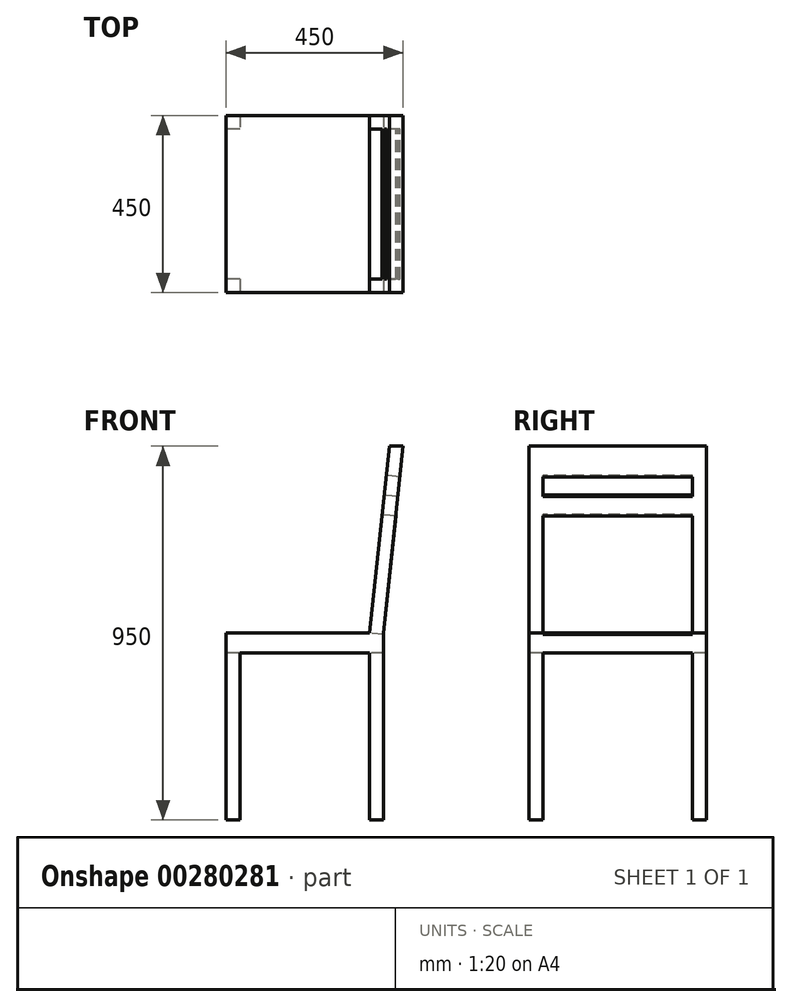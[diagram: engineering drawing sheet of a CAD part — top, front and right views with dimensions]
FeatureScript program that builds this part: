
annotation { "Feature Type Name" : "Feature", "Feature Type Description" : "" }
export const myFeature = defineFeature(function(context is Context, id is Id, definition is map)
    precondition{}
    {
        {
            var Q0;
            Q0=qCreatedBy(makeId("Top.planeOp"),FACE);
            var sketch = newSketch(context, id + "F0", { "sketchPlane" : qUnion([Q0])});
            skLineSegment(sketch, "E0.bottom", {"start": v(225, 225) * mm, "end": v(-225, 225) * mm});
            skLineSegment(sketch, "E0.top", {"start": v(225, -225) * mm, "end": v(-225, -225) * mm});
            skLineSegment(sketch, "E0.left", {"start": v(225, 225) * mm, "end": v(225, -225) * mm});
            skLineSegment(sketch, "E0.right", {"start": v(-225, 225) * mm, "end": v(-225, -225) * mm});
            skPoint(sketch, "E0.middle", {"position": v(0, 0) * mm});
            skSolve(sketch);
        }
        {
            var Q0;
            Q0=qSketchRegion(id+"F0",true);
            extrude(context, id + "F1", {"entities" : qUnion([Q0]), "depth" : 950 * mm});
        }
        {
            var Q0;
            Q0=makeQuery(id+"F1.opExtrude","SWEPT_FACE",FACE,{"disambiguationData":[OSD([sQuery(id+"F0.wireOp",EDGE,"E0.top")])]});
            var sketch = newSketch(context, id + "F2", { "sketchPlane" : qUnion([Q0])});
            skLineSegment(sketch, "E1.bottom", {"start": v(-225, 475) * mm, "end": v(225, 475) * mm});
            skLineSegment(sketch, "E1.top", {"start": v(-225, 425) * mm, "end": v(225, 425) * mm});
            skLineSegment(sketch, "E1.left", {"start": v(-225, 475) * mm, "end": v(-225, 425) * mm});
            skLineSegment(sketch, "E1.right", {"start": v(225, 475) * mm, "end": v(225, 425) * mm});
            skLineSegment(sketch, "E2", {"start": v(175, 475) * mm, "end": v(225, 950) * mm});
            skLineSegment(sketch, "E3", {"start": v(140, 475) * mm, "end": v(190, 950) * mm});
            skLineSegment(sketch, "E4", {"start": v(140, 475) * mm, "end": v(140, 0) * mm});
            skLineSegment(sketch, "E5", {"start": v(175, 475) * mm, "end": v(175, 0) * mm});
            skLineSegment(sketch, "E6", {"start": v(-190, 425) * mm, "end": v(-190, 0) * mm});
            skSolve(sketch);
        }
        {
            var Q0;
            {var subQ4=sQuery(id+"F2.wireOp",EDGE,"E3");Q0=makeQuery(id+"F2.imprint","IMPRINT",FACE,{"disambiguationData":[TD([[makeQuery(id+"F2.imprint","IMPRINT",EDGE,{"derivedFrom":subQ4}),1.0]])]});}
            var Q1;
            {var subQ0=sQuery(id+"F2.wireOp",EDGE,"E6");Q1=makeQuery(id+"F2.imprint","IMPRINT",FACE,{"disambiguationData":[TD([[makeQuery(id+"F2.imprint","IMPRINT",EDGE,{"derivedFrom":subQ0}),1.0]])]});}
            var Q2;
            {var subQ1=sQuery(id+"F0.wireOp",EDGE,"E0.top");var subQ4=sQuery(id+"F2.wireOp",EDGE,"E5");var subQ6=makeQuery(id+"F1.opExtrude","CAP_EDGE",EDGE,{"disambiguationData":[OSD([subQ1])],"isStart":true});var subQ7=makeQuery(id+"F2.imprint","INTERSECT",VERTEX,{"derivedFrom":[subQ6,subQ4]});Q2=makeQuery(id+"F2.imprint","IMPRINT",FACE,{"disambiguationData":[TD([[makeQuery(id+"F2.imprint","IMPRINT",EDGE,{"disambiguationData":[TD([[subQ7,1.0]])],"derivedFrom":subQ4}),1.0]])]});}
            var Q3;
            {var subQ0=sQuery(id+"F2.wireOp",EDGE,"E1.right");Q3=makeQuery(id+"F2.imprint","IMPRINT",FACE,{"disambiguationData":[TD([[makeQuery(id+"F2.imprint","IMPRINT",EDGE,{"derivedFrom":subQ0}),-1.0]])]});}
            var Q4;
            {var subQ4=sQuery(id+"F2.wireOp",EDGE,"E2");Q4=makeQuery(id+"F2.imprint","IMPRINT",FACE,{"disambiguationData":[TD([[makeQuery(id+"F2.imprint","IMPRINT",EDGE,{"derivedFrom":subQ4}),-1.0]])]});}
            extrude(context, id + "F3", {"entities" : qUnion([Q0, Q1, Q2, Q3, Q4]), "operationType" : NewBodyOperationType.REMOVE, "endBound" : BoundingType.THROUGH_ALL, "oppositeDirection" : true, "depth" : 25 * mm});
        }
        {
            var Q0;
            Q0=makeQuery(id+"F1.opExtrude","SWEPT_FACE",FACE,{"disambiguationData":[OSD([sQuery(id+"F0.wireOp",EDGE,"E0.right")])]});
            var sketch = newSketch(context, id + "F4", { "sketchPlane" : qUnion([Q0])});
            skLineSegment(sketch, "E7.bottom", {"start": v(-190, 0) * mm, "end": v(190, 0) * mm});
            skLineSegment(sketch, "E7.top", {"start": v(-190, 425) * mm, "end": v(190, 425) * mm});
            skLineSegment(sketch, "E7.left", {"start": v(-190, 0) * mm, "end": v(-190, 425) * mm});
            skLineSegment(sketch, "E7.right", {"start": v(190, 0) * mm, "end": v(190, 425) * mm});
            skSolve(sketch);
        }
        {
            var Q0;
            Q0=makeQuery(id+"F4.imprint","IMPRINT",FACE,{"disambiguationData":[TD([[makeQuery(id+"F4.imprint","IMPRINT",EDGE,{"derivedFrom":sQuery(id+"F4.wireOp",EDGE,"E7.bottom")}),1.0]])]});
            extrude(context, id + "F5", {"entities" : qUnion([Q0]), "operationType" : NewBodyOperationType.REMOVE, "endBound" : BoundingType.THROUGH_ALL, "oppositeDirection" : true, "depth" : 25 * mm});
        }
        {
            var Q0;
            Q0=makeQuery(id+"F3.boolean.opBoolean","COPY",FACE,{"derivedFrom":makeQuery(id+"F3.opExtrude","SWEPT_FACE",FACE,{"disambiguationData":[OSD([sQuery(id+"F2.wireOp",EDGE,"E3")])]})});
            var sketch = newSketch(context, id + "F6", { "sketchPlane" : qUnion([Q0])});
            skLineSegment(sketch, "E8", {"start": v(-190, 487.05) * mm, "end": v(-190, 889.67) * mm});
            skLineSegment(sketch, "E9", {"start": v(-190, 889.67) * mm, "end": v(190, 889.67) * mm});
            skLineSegment(sketch, "E10", {"start": v(190, 889.67) * mm, "end": v(190, 487.05) * mm});
            skLineSegment(sketch, "E11", {"start": v(-190, 789.67) * mm, "end": v(190, 789.67) * mm});
            skLineSegment(sketch, "E12", {"start": v(-190, 839.67) * mm, "end": v(190, 839.67) * mm});
            skSolve(sketch);
        }
        {
            var Q0;
            {var subQ3=sQuery(id+"F6.wireOp",EDGE,"E11");Q0=makeQuery(id+"F6.imprint","IMPRINT",FACE,{"disambiguationData":[TD([[makeQuery(id+"F6.imprint","IMPRINT",EDGE,{"derivedFrom":subQ3}),-1.0]])]});}
            var Q1;
            {var subQ0=sQuery(id+"F6.wireOp",EDGE,"E9");Q1=makeQuery(id+"F6.imprint","IMPRINT",FACE,{"disambiguationData":[TD([[makeQuery(id+"F6.imprint","IMPRINT",EDGE,{"derivedFrom":subQ0}),-1.0]])]});}
            extrude(context, id + "F7", {"entities" : qUnion([Q0, Q1]), "operationType" : NewBodyOperationType.REMOVE, "endBound" : BoundingType.THROUGH_ALL, "oppositeDirection" : true, "depth" : 25 * mm});
        }
    });
